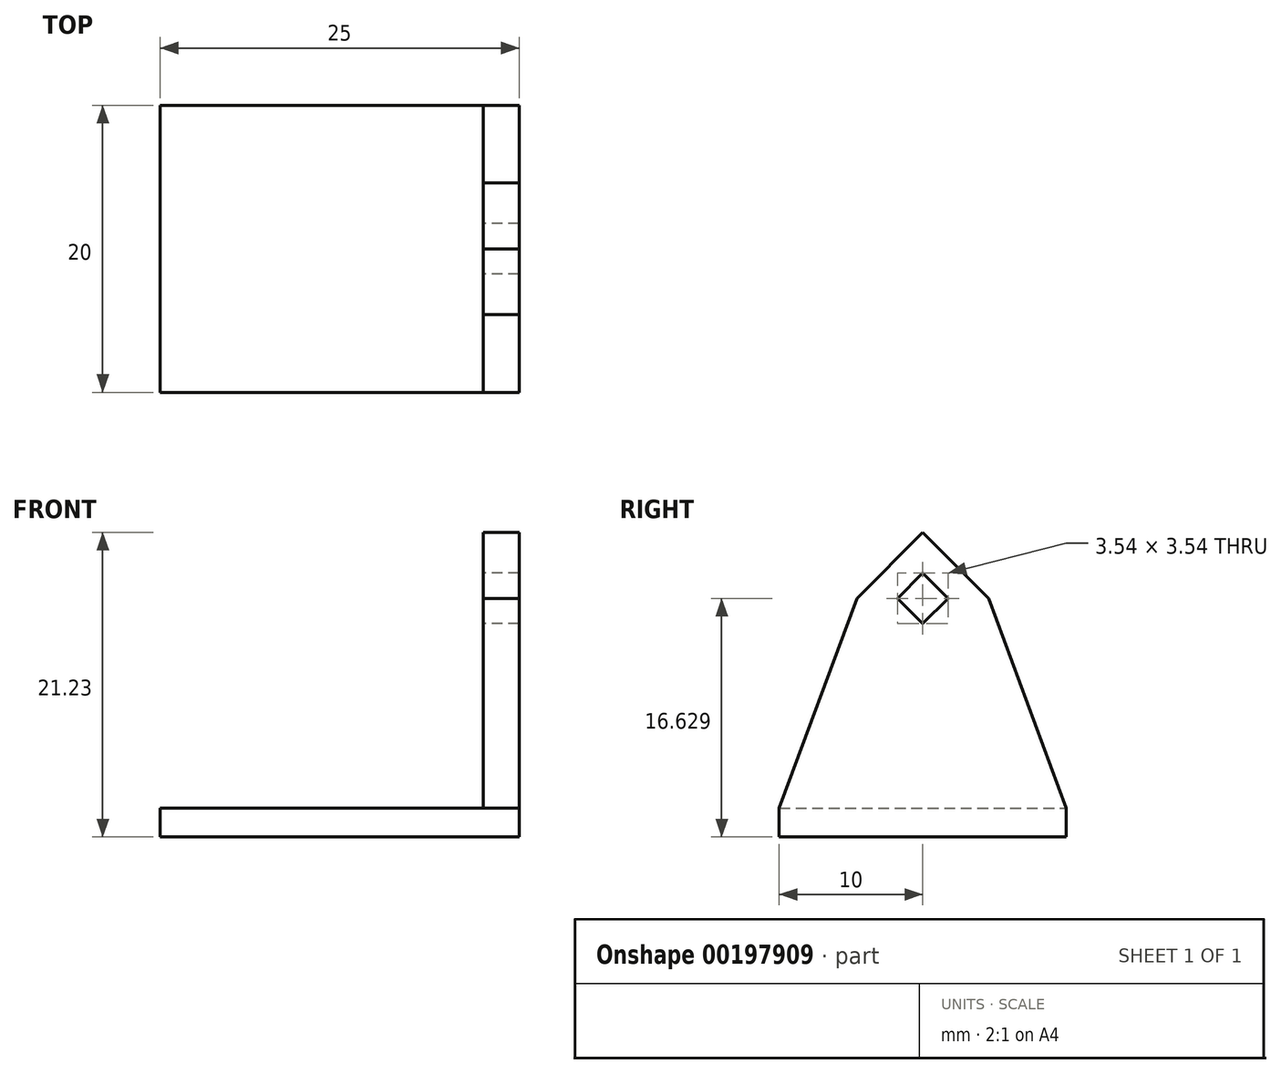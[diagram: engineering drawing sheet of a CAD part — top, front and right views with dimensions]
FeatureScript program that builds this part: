
annotation { "Feature Type Name" : "Feature", "Feature Type Description" : "" }
export const myFeature = defineFeature(function(context is Context, id is Id, definition is map)
    precondition{}
    {
        {
            var Q0;
            Q0=qCreatedBy(makeId("Right.planeOp"),FACE);
            cPlane(context, id + "F0", {"entities" : qUnion([Q0]), "cplaneType" : CPlaneType.OFFSET, "offset" : 10 * mm, "width" : 150 * mm, "height" : 150 * mm});
        }
        {
            var Q0;
            Q0=qCreatedBy(id+"F0.planeOp",FACE);
            var sketch = newSketch(context, id + "F1", { "sketchPlane" : qUnion([Q0])});
            skCircle(sketch, "E0", {"center": v(0, 14.63) * mm, "radius": 1.25 * mm, "construction": true});
            skLineSegment(sketch, "E1", {"start": v(-10, 0) * mm, "end": v(10, 0) * mm});
            skLineSegment(sketch, "E2", {"start": v(10, 0) * mm, "end": v(4.6, 14.63) * mm});
            skLineSegment(sketch, "E3.MirrorCS", {"start": v(-10, 0) * mm, "end": v(-4.6, 14.63) * mm});
            skLineSegment(sketch, "E4.bottom", {"start": v(1.77, 14.63) * mm, "end": v(0, 16.4) * mm});
            skLineSegment(sketch, "E4.top", {"start": v(0, 12.86) * mm, "end": v(-1.77, 14.63) * mm});
            skLineSegment(sketch, "E4.left", {"start": v(1.77, 14.63) * mm, "end": v(0, 12.86) * mm});
            skLineSegment(sketch, "E4.right", {"start": v(0, 16.4) * mm, "end": v(-1.77, 14.63) * mm});
            skLineSegment(sketch, "E5", {"start": v(4.6, 14.63) * mm, "end": v(0, 19.23) * mm});
            skLineSegment(sketch, "E6", {"start": v(0, 19.23) * mm, "end": v(-4.6, 14.63) * mm});
            skSolve(sketch);
        }
        {
            var Q0;
            Q0 = qSketchRegion(id + "F1", true);
            extrude(context, id + "F2", {"entities" : qUnion([Q0]), "depth" : 2.5 * mm});
        }
        {
            var Q0;
            Q0=qCreatedBy(makeId("Top.planeOp"),FACE);
            var sketch = newSketch(context, id + "F3", { "sketchPlane" : qUnion([Q0])});
            skLineSegment(sketch, "E7.bottom", {"start": v(-12.5, -10) * mm, "end": v(12.5, -10) * mm});
            skLineSegment(sketch, "E7.top", {"start": v(-12.5, 10) * mm, "end": v(12.5, 10) * mm});
            skLineSegment(sketch, "E7.left", {"start": v(-12.5, -10) * mm, "end": v(-12.5, 10) * mm});
            skLineSegment(sketch, "E7.right", {"start": v(12.5, -10) * mm, "end": v(12.5, 10) * mm});
            skSolve(sketch);
        }
        {
            var Q0;
            Q0 = qSketchRegion(id + "F3", true);
            extrude(context, id + "F4", {"entities" : qUnion([Q0]), "operationType" : NewBodyOperationType.ADD, "oppositeDirection" : true, "depth" : 2 * mm});
        }
    });
